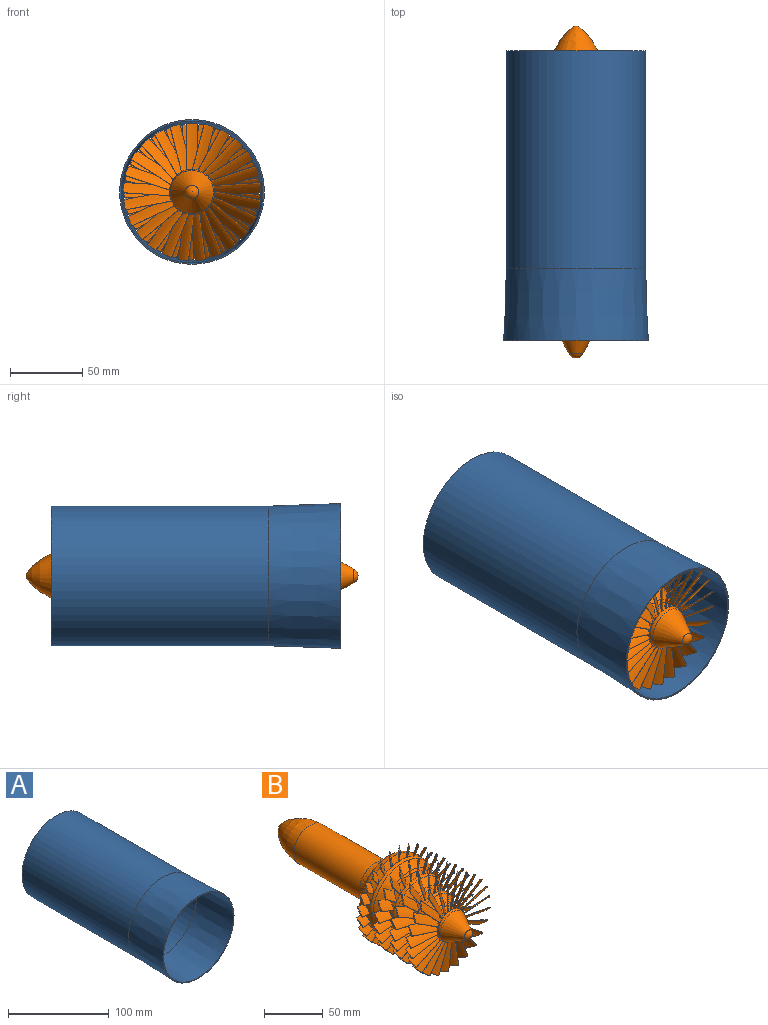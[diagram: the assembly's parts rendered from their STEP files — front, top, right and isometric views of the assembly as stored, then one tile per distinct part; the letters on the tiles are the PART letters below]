
ASSEMBLY  parts=2 mates=1
PART A: 6 faces, bbox 100x200x100 mm
  f0: cone r=50mm half-angle=2deg, axis (0,-1,0), area 15443.1mm2, adj f1,f5
  f1: plane 100x100mm, normal (0,-1,0), area 311mm2, adj f0,f2
  f2: cone r=49mm half-angle=2deg, axis (0,-1,0), area 15128.8mm2, adj f1,f3
  f3: cylinder r=47.25mm len=150mm, axis (0,-1,0), area 44535.8mm2, adj f2,f4
  f4: plane 96.51x96.51mm, normal (0,1,0), area 300mm2, adj f3,f5
  f5: cylinder r=48.25mm len=150mm, axis (0,-1,0), area 45478.3mm2, adj f0,f4
PART B: 370 faces, bbox 95.2x229.3x95.1 mm
  f0: cylinder r=22.77mm len=10.61mm, axis (0,-1,0), area 35.7mm2, adj f178,f180,f367,f369
  f1: cylinder r=22.77mm len=11.53mm, axis (0,-1,0), area 35.7mm2, adj f181,f183,f367,f369
  f2: cylinder r=22.77mm len=11.73mm, axis (0,-1,0), area 30.5mm2, adj f184,f186,f367,f368,f369
  f3: cylinder r=22.77mm len=11.19mm, axis (0,-1,0), area 35.7mm2, adj f187,f189,f367,f369
  f4: cylinder r=22.77mm len=9.95mm, axis (0,-1,0), area 35.7mm2, adj f190,f192,f367,f369
  f5: cylinder r=22.77mm len=8.53mm, axis (0,-1,0), area 35.7mm2, adj f193,f195,f367,f369
  f6: cylinder r=22.77mm len=10.27mm, axis (0,-1,0), area 35.7mm2, adj f196,f198,f367,f369
  f7: cylinder r=22.77mm len=11.37mm, axis (0,-1,0), area 35.7mm2, adj f199,f201,f367,f369
  f8: cylinder r=22.77mm len=11.75mm, axis (0,-1,0), area 35.7mm2, adj f202,f204,f367,f369
  f9: cylinder r=22.77mm len=11.39mm, axis (0,-1,0), area 35.7mm2, adj f205,f207,f367,f369
  f10: cylinder r=22.77mm len=10.32mm, axis (0,-1,0), area 35.7mm2, adj f208,f210,f367,f369
  f11: cylinder r=22.77mm len=8.6mm, axis (0,-1,0), area 35.7mm2, adj f142,f209,f367,f369
  f12: cylinder r=22.77mm len=9.9mm, axis (0,-1,0), area 35.7mm2, adj f139,f141,f367,f369
  f13: cylinder r=22.77mm len=11.16mm, axis (0,-1,0), area 35.7mm2, adj f138,f147,f367,f369
  f14: cylinder r=22.77mm len=11.72mm, axis (0,-1,0), area 30.5mm2, adj f148,f150,f367,f369
  f15: cylinder r=22.77mm len=11.55mm, axis (0,-1,0), area 35.7mm2, adj f145,f151,f367,f369
  f16: cylinder r=22.77mm len=10.65mm, axis (0,-1,0), area 35.7mm2, adj f144,f159,f367,f369
  f17: cylinder r=22.77mm len=9.08mm, axis (0,-1,0), area 35.7mm2, adj f160,f162,f367,f369
  f18: cylinder r=22.77mm len=9.48mm, axis (0,-1,0), area 35.7mm2, adj f157,f163,f367,f369
  f19: cylinder r=22.77mm len=10.91mm, axis (0,-1,0), area 35.7mm2, adj f154,f156,f367,f369
  f20: cylinder r=22.77mm len=11.65mm, axis (0,-1,0), area 35.7mm2, adj f153,f166,f367,f369
  f21: cylinder r=22.77mm len=11.66mm, axis (0,-1,0), area 35.7mm2, adj f165,f169,f367,f369
  f22: cylinder r=22.77mm len=10.94mm, axis (0,-1,0), area 35.7mm2, adj f168,f172,f367,f369
  f23: cylinder r=22.77mm len=9.53mm, axis (0,-1,0), area 35.7mm2, adj f171,f175,f367,f369
  f24: cylinder r=30.05mm len=12.66mm, axis (0,-1,0), area 48mm2, adj f328,f330,f365,f366
  f25: cylinder r=30.05mm len=13.49mm, axis (0,-1,0), area 48mm2, adj f331,f333,f365,f366
  f26: cylinder r=30.05mm len=13.47mm, axis (0,-1,0), area 48mm2, adj f334,f336,f365,f366
  f27: cylinder r=30.05mm len=12.6mm, axis (0,-1,0), area 48mm2, adj f337,f339,f365,f366
  f28: cylinder r=30.05mm len=10.95mm, axis (0,-1,0), area 48mm2, adj f340,f342,f365,f366
  f29: cylinder r=30.05mm len=10.52mm, axis (0,-1,0), area 48mm2, adj f343,f345,f365,f366
  f30: cylinder r=30.05mm len=12.33mm, axis (0,-1,0), area 48mm2, adj f346,f348,f365,f366
  f31: cylinder r=30.05mm len=13.36mm, axis (0,-1,0), area 48mm2, adj f349,f351,f365,f366
  f32: cylinder r=30.05mm len=13.55mm, axis (0,-1,0), area 48mm2, adj f352,f354,f365,f366
  f33: cylinder r=30.05mm len=12.9mm, axis (0,-1,0), area 48mm2, adj f355,f357,f365,f366
  f34: cylinder r=30.05mm len=11.43mm, axis (0,-1,0), area 48mm2, adj f358,f360,f365,f366
  f35: cylinder r=30.05mm len=9.96mm, axis (0,-1,0), area 48mm2, adj f291,f359,f365,f366
  f36: cylinder r=30.05mm len=11.94mm, axis (0,-1,0), area 48mm2, adj f288,f292,f365,f366
  f37: cylinder r=30.05mm len=13.18mm, axis (0,-1,0), area 48mm2, adj f289,f297,f365,f366
  f38: cylinder r=30.05mm len=13.59mm, axis (0,-1,0), area 48mm2, adj f298,f300,f365,f366
  f39: cylinder r=30.05mm len=13.14mm, axis (0,-1,0), area 48mm2, adj f294,f301,f365,f366
  f40: cylinder r=30.05mm len=11.87mm, axis (0,-1,0), area 48mm2, adj f295,f309,f365,f366
  f41: cylinder r=30.05mm len=9.85mm, axis (0,-1,0), area 48mm2, adj f310,f312,f365,f366
  f42: cylinder r=30.05mm len=11.51mm, axis (0,-1,0), area 48mm2, adj f306,f313,f365,f366
  f43: cylinder r=30.05mm len=12.95mm, axis (0,-1,0), area 48mm2, adj f303,f307,f365,f366
  f44: cylinder r=30.05mm len=13.56mm, axis (0,-1,0), area 48mm2, adj f304,f316,f365,f366
  f45: cylinder r=30.05mm len=13.33mm, axis (0,-1,0), area 48mm2, adj f315,f319,f365,f366
  f46: cylinder r=30.05mm len=12.26mm, axis (0,-1,0), area 48mm2, adj f318,f322,f365,f366
  f47: cylinder r=30.05mm len=10.42mm, axis (0,-1,0), area 48mm2, adj f321,f325,f365,f366
  f48: cylinder r=30.05mm len=11.04mm, axis (0,-1,0), area 48mm2, adj f324,f327,f365,f366
  f49: cylinder r=37.33mm len=74.66mm, axis (0,-1,0), area 1745mm2, adj f50,f59,f213,f214,f216,f217,f219,f220
  f50: cylinder r=37.33mm len=6.36mm, axis (0,-1,0), area 18.9mm2, adj f49,f258,f364
  f51: cylinder r=22.77mm len=9.02mm, axis (0,-1,0), area 35.7mm2, adj f174,f177,f367,f369
  f52: cylinder r=15.49mm len=30.98mm, axis (0,-1,0), area 575mm2, adj f53,f63,f64,f66,f67,f69,f70,f72
  f53: cylinder r=15.49mm len=3.79mm, axis (0,-1,0), area 6.1mm2, adj f52,f96,f100,f362
  f54: cone r=22.77mm half-angle=36.1deg, axis (0,1,0), area 1095.6mm2, adj f362,f369
  f55: cone r=15.49mm half-angle=28.8deg, axis (0,1,0), area 1297.2mm2, adj f56,f363
  f56: sphere r=5.39mm, area 94.4mm2, adj f55
  f57: revolved ~39.03x38.98mm, area 3530.5mm2, adj f58
  f58: cylinder r=19.54mm len=78.57mm, axis (0,-1,0), area 9647.2mm2, adj f57,f59
  f59: revolved ~74.66x74.66mm, area 5313.1mm2, adj f49,f58
  f60: cone r=37.33mm half-angle=36.1deg, axis (0,1,0), area 1929.3mm2, adj f364,f365
  f61: cone r=30.05mm half-angle=36.1deg, axis (0,1,0), area 1512.5mm2, adj f366,f367
  f62: cone r=49mm half-angle=2deg, axis (0,-1,0), area 4.1mm2, adj f63,f64
  f63: extruded ~33.09x14.94mm, area 321.3mm2, adj f52,f62,f64,f362
  f64: extruded ~33.12x14.9mm, area 321.3mm2, adj f52,f62,f63,f362
  f65: cone r=49mm half-angle=2deg, axis (0,-1,0), area 4.1mm2, adj f66,f67
  f66: extruded ~31.77x21.82mm, area 321.3mm2, adj f52,f65,f67,f362
  f67: extruded ~31.78x21.8mm, area 321.3mm2, adj f52,f65,f66,f362
  f68: cone r=49mm half-angle=2deg, axis (0,-1,0), area 4.1mm2, adj f69,f70
  f69: extruded ~28.45x27.33mm, area 321.3mm2, adj f52,f68,f70,f362
  f70: extruded ~28.45x27.32mm, area 321.3mm2, adj f52,f68,f69,f362
  f71: cone r=49mm half-angle=2deg, axis (0,-1,0), area 4.1mm2, adj f72,f73
  f72: extruded ~31.12x23.34mm, area 321.3mm2, adj f52,f71,f73,f362
  f73: extruded ~31.13x23.32mm, area 321.3mm2, adj f52,f71,f72,f362
  f74: cone r=49mm half-angle=2deg, axis (0,-1,0), area 4.1mm2, adj f75,f76
  f75: extruded ~32.96x16.76mm, area 321.3mm2, adj f52,f74,f76,f362
  f76: extruded ~32.98x16.73mm, area 321.3mm2, adj f52,f74,f75,f362
  f77: cone r=49mm half-angle=2deg, axis (0,-1,0), area 4.1mm2, adj f78,f79
  f78: extruded ~32.72x9.13mm, area 321.3mm2, adj f52,f77,f79,f362
  f79: extruded ~32.76x9.09mm, area 321.3mm2, adj f52,f77,f78,f362
  f80: cone r=49mm half-angle=2deg, axis (0,-1,0), area 4.1mm2, adj f81,f82
  f81: extruded ~33.1x13.05mm, area 321.3mm2, adj f52,f80,f82,f362
  f82: extruded ~33.13x13.01mm, area 321.3mm2, adj f52,f80,f81,f362
  f83: cone r=49mm half-angle=2deg, axis (0,-1,0), area 4.1mm2, adj f84,f85
  f84: extruded ~32.29x20.21mm, area 321.3mm2, adj f52,f83,f85,f362
  f85: extruded ~32.31x20.19mm, area 321.3mm2, adj f52,f83,f84,f362
  f86: cone r=49mm half-angle=2deg, axis (0,-1,0), area 4.1mm2, adj f87,f88
  f87: extruded ~29.45x26.1mm, area 321.3mm2, adj f52,f86,f88,f362
  f88: extruded ~29.46x26.09mm, area 321.3mm2, adj f52,f86,f87,f362
  f89: cone r=49mm half-angle=2deg, axis (0,-1,0), area 4.1mm2, adj f90,f91
  f90: extruded ~30.35x24.77mm, area 321.3mm2, adj f52,f89,f91,f362
  f91: extruded ~30.35x24.76mm, area 321.3mm2, adj f52,f89,f90,f362
  f92: cone r=49mm half-angle=2deg, axis (0,-1,0), area 4.1mm2, adj f93,f94
  f93: extruded ~32.69x18.52mm, area 321.3mm2, adj f52,f92,f94,f362
  f94: extruded ~32.71x18.5mm, area 321.3mm2, adj f52,f92,f93,f362
  f95: cone r=49mm half-angle=2deg, axis (0,-1,0), area 4.1mm2, adj f96,f97
  f96: extruded ~32.97x11.11mm, area 321.7mm2, adj f52,f53,f95,f97,f362
  f97: extruded ~33.01x11.07mm, area 321.3mm2, adj f52,f95,f96,f362
  f98: cone r=49mm half-angle=2deg, axis (0,-1,0), area 4.1mm2, adj f99,f100
  f99: extruded ~32.98x11.11mm, area 321.3mm2, adj f52,f98,f100,f362
  f100: extruded ~33.01x11.07mm, area 321.3mm2, adj f52,f53,f98,f99,f362
  f101: cone r=49mm half-angle=2deg, axis (0,-1,0), area 4.1mm2, adj f102,f103
  f102: extruded ~32.71x18.5mm, area 321.3mm2, adj f52,f101,f103,f362
  f103: extruded ~32.69x18.52mm, area 321.3mm2, adj f52,f101,f102,f362
  f104: cone r=49mm half-angle=2deg, axis (0,-1,0), area 4.1mm2, adj f105,f106
  f105: extruded ~30.35x24.76mm, area 321.3mm2, adj f52,f104,f106,f362
  f106: extruded ~30.35x24.77mm, area 321.3mm2, adj f52,f104,f105,f362
  f107: cone r=49mm half-angle=2deg, axis (0,-1,0), area 4.1mm2, adj f108,f109
  f108: extruded ~29.46x26.09mm, area 321.3mm2, adj f52,f107,f109,f362
  f109: extruded ~29.45x26.1mm, area 321.3mm2, adj f52,f107,f108,f362
  f110: cone r=49mm half-angle=2deg, axis (0,-1,0), area 4.1mm2, adj f111,f112
  f111: extruded ~32.31x20.19mm, area 321.3mm2, adj f52,f110,f112,f362
  f112: extruded ~32.29x20.21mm, area 321.3mm2, adj f52,f110,f111,f362
  f113: cone r=49mm half-angle=2deg, axis (0,-1,0), area 4.1mm2, adj f114,f115
  f114: extruded ~33.13x13.01mm, area 321.3mm2, adj f52,f113,f115,f362
  f115: extruded ~33.1x13.05mm, area 321.3mm2, adj f52,f113,f114,f362
  f116: cone r=49mm half-angle=2deg, axis (0,-1,0), area 4.1mm2, adj f117,f118
  f117: extruded ~32.76x9.09mm, area 321.3mm2, adj f52,f116,f118,f362
  f118: extruded ~32.72x9.13mm, area 321.3mm2, adj f52,f116,f117,f362
  f119: cone r=49mm half-angle=2deg, axis (0,-1,0), area 4.1mm2, adj f120,f121
  f120: extruded ~32.98x16.73mm, area 321.3mm2, adj f52,f119,f121,f362
  f121: extruded ~32.96x16.76mm, area 321.3mm2, adj f52,f119,f120,f362
  f122: cone r=49mm half-angle=2deg, axis (0,-1,0), area 4.1mm2, adj f123,f124
  f123: extruded ~31.13x23.32mm, area 321.3mm2, adj f52,f122,f124,f362
  f124: extruded ~31.12x23.34mm, area 321.3mm2, adj f52,f122,f123,f362
  f125: cone r=49mm half-angle=2deg, axis (0,-1,0), area 4.1mm2, adj f126,f127
  f126: extruded ~28.45x27.32mm, area 321.3mm2, adj f52,f125,f127,f362
  f127: extruded ~28.45x27.33mm, area 321.3mm2, adj f52,f125,f126,f362
  f128: cone r=49mm half-angle=2deg, axis (0,-1,0), area 4.1mm2, adj f129,f130
  f129: extruded ~31.78x21.8mm, area 321.3mm2, adj f52,f128,f130,f362
  f130: extruded ~31.77x21.82mm, area 321.3mm2, adj f52,f128,f129,f362
  f131: cone r=49mm half-angle=2deg, axis (0,-1,0), area 4.1mm2, adj f132,f133
  f132: extruded ~33.12x14.9mm, area 321.3mm2, adj f52,f131,f133,f362
  f133: extruded ~33.09x14.94mm, area 321.3mm2, adj f52,f131,f132,f362
  f134: extruded ~32.34x7.12mm, area 321.3mm2, adj f52,f135,f136,f362
  f135: extruded ~32.38x7.12mm, area 321.3mm2, adj f52,f134,f136,f362
  f136: cone r=49mm half-angle=2deg, axis (0,-1,0), area 4.1mm2, adj f134,f135
  f137: cone r=49mm half-angle=2deg, axis (0,-1,0), area 4.1mm2, adj f138,f139
  f138: extruded ~24.97x16.62mm, area 240.7mm2, adj f13,f137,f139,f367,f369
  f139: extruded ~25x16.6mm, area 240.8mm2, adj f12,f137,f138,f367,f369
  f140: cone r=49mm half-angle=2deg, axis (0,-1,0), area 4.1mm2, adj f141,f142
  f141: extruded ~23.27x20.83mm, area 240.7mm2, adj f12,f140,f142,f367,f369
  f142: extruded ~23.28x20.82mm, area 240.8mm2, adj f11,f140,f141,f367,f369
  f143: cone r=49mm half-angle=2deg, axis (0,-1,0), area 4.1mm2, adj f144,f145
  f144: extruded ~25.23x14.4mm, area 240.7mm2, adj f16,f143,f145,f367,f369
  f145: extruded ~25.27x14.37mm, area 240.8mm2, adj f15,f143,f144,f367,f369
  f146: cone r=49mm half-angle=2deg, axis (0,-1,0), area 4.1mm2, adj f147,f148
  f147: extruded ~25.15x11.34mm, area 240.8mm2, adj f13,f146,f148,f367,f369
  f148: extruded ~25.11x11.37mm, area 240.7mm2, adj f14,f146,f147,f367,f369
  f149: cone r=49mm half-angle=2deg, axis (0,-1,0), area 4.1mm2, adj f150,f151
  f150: extruded ~24.71x8.75mm, area 240.8mm2, adj f14,f149,f151,f367,f369
  f151: extruded ~24.66x8.79mm, area 240.7mm2, adj f15,f149,f150,f367,f369
  f152: cone r=49mm half-angle=2deg, axis (0,-1,0), area 4.1mm2, adj f153,f154
  f153: extruded ~25.22x12.77mm, area 240.7mm2, adj f20,f152,f154,f367,f369
  f154: extruded ~25.26x12.73mm, area 240.8mm2, adj f19,f152,f153,f367,f369
  f155: cone r=49mm half-angle=2deg, axis (0,-1,0), area 4.1mm2, adj f156,f157
  f156: extruded ~24.69x17.78mm, area 240.7mm2, adj f19,f155,f157,f367,f369
  f157: extruded ~24.72x17.77mm, area 240.8mm2, adj f18,f155,f156,f367,f369
  f158: cone r=49mm half-angle=2deg, axis (0,-1,0), area 4.1mm2, adj f159,f160
  f159: extruded ~24.24x19.09mm, area 240.8mm2, adj f16,f158,f160,f367,f369
  f160: extruded ~24.22x19.1mm, area 240.7mm2, adj f17,f158,f159,f367,f369
  f161: cone r=49mm half-angle=2deg, axis (0,-1,0), area 4.1mm2, adj f162,f163
  f162: extruded ~22.62x21.68mm, area 240.8mm2, adj f17,f161,f163,f367,f369
  f163: extruded ~22.61x21.68mm, area 240.7mm2, adj f18,f161,f162,f367,f369
  f164: cone r=49mm half-angle=2deg, axis (0,-1,0), area 4.1mm2, adj f165,f166
  f165: extruded ~24.27x7.29mm, area 240.7mm2, adj f21,f164,f166,f367,f369
  f166: extruded ~24.32x7.24mm, area 240.8mm2, adj f20,f164,f165,f367,f369
  f167: cone r=49mm half-angle=2deg, axis (0,-1,0), area 4.1mm2, adj f168,f169
  f168: extruded ~25.24x13.07mm, area 240.7mm2, adj f22,f167,f169,f367,f369
  f169: extruded ~25.28x13.04mm, area 240.8mm2, adj f21,f167,f168,f367,f369
  f170: cone r=49mm half-angle=2deg, axis (0,-1,0), area 4.1mm2, adj f171,f172
  f171: extruded ~24.62x18.03mm, area 240.7mm2, adj f23,f170,f172,f367,f369
  f172: extruded ~24.64x18.02mm, area 240.8mm2, adj f22,f170,f171,f367,f369
  f173: cone r=49mm half-angle=2deg, axis (0,-1,0), area 4.1mm2, adj f174,f175
  f174: extruded ~22.45x21.86mm, area 240.7mm2, adj f51,f173,f175,f367,f369
  f175: extruded ~22.46x21.86mm, area 240.8mm2, adj f23,f173,f174,f367,f369
  f176: cone r=49mm half-angle=2deg, axis (0,-1,0), area 4.1mm2, adj f177,f178
  f177: extruded ~24.33x18.86mm, area 240.8mm2, adj f51,f176,f178,f367,f369
  f178: extruded ~24.31x18.87mm, area 240.7mm2, adj f0,f176,f177,f367,f369
  f179: cone r=49mm half-angle=2deg, axis (0,-1,0), area 4.1mm2, adj f180,f181
  f180: extruded ~25.28x14.08mm, area 240.8mm2, adj f0,f179,f181,f367,f369
  f181: extruded ~25.24x14.11mm, area 240.7mm2, adj f1,f179,f180,f367,f369
  f182: cone r=49mm half-angle=2deg, axis (0,-1,0), area 4.1mm2, adj f183,f184
  f183: extruded ~24.63x8.42mm, area 240.8mm2, adj f1,f182,f184,f367,f369
  f184: extruded ~24.58x8.46mm, area 240.7mm2, adj f2,f182,f183,f367,f369
  f185: cone r=49mm half-angle=2deg, axis (0,-1,0), area 4.1mm2, adj f186,f187
  f186: extruded ~25.19x11.65mm, area 240.8mm2, adj f2,f185,f187,f368,f369
  f187: extruded ~25.14x11.69mm, area 240.7mm2, adj f3,f185,f186,f367,f369
  f188: cone r=49mm half-angle=2deg, axis (0,-1,0), area 4.1mm2, adj f189,f190
  f189: extruded ~24.95x16.87mm, area 240.8mm2, adj f3,f188,f190,f367,f369
  f190: extruded ~24.92x16.89mm, area 240.7mm2, adj f4,f188,f189,f367,f369
  f191: cone r=49mm half-angle=2deg, axis (0,-1,0), area 4.1mm2, adj f192,f193
  f192: extruded ~23.14x21.02mm, area 240.8mm2, adj f4,f191,f193,f367,f369
  f193: extruded ~23.13x21.02mm, area 240.7mm2, adj f5,f191,f192,f367,f369
  f194: cone r=49mm half-angle=2deg, axis (0,-1,0), area 4.1mm2, adj f195,f196
  f195: extruded ~23.85x19.88mm, area 240.8mm2, adj f5,f194,f196,f367,f369
  f196: extruded ~23.84x19.89mm, area 240.7mm2, adj f6,f194,f195,f367,f369
  f197: cone r=49mm half-angle=2deg, axis (0,-1,0), area 4.1mm2, adj f198,f199
  f198: extruded ~25.19x15.37mm, area 240.8mm2, adj f6,f197,f199,f367,f369
  f199: extruded ~25.16x15.4mm, area 240.7mm2, adj f7,f197,f198,f367,f369
  f200: cone r=49mm half-angle=2deg, axis (0,-1,0), area 4.1mm2, adj f201,f202
  f201: extruded ~24.94x9.9mm, area 240.8mm2, adj f7,f200,f202,f367,f369
  f202: extruded ~24.89x9.94mm, area 240.7mm2, adj f8,f200,f201,f367,f369
  f203: cone r=49mm half-angle=2deg, axis (0,-1,0), area 4.1mm2, adj f204,f205
  f204: extruded ~25x10.22mm, area 240.8mm2, adj f8,f203,f205,f367,f369
  f205: extruded ~24.95x10.26mm, area 240.7mm2, adj f9,f203,f204,f367,f369
  f206: cone r=49mm half-angle=2deg, axis (0,-1,0), area 4.1mm2, adj f207,f208
  f207: extruded ~25.16x15.65mm, area 240.8mm2, adj f9,f206,f208,f367,f369
  f208: extruded ~25.12x15.67mm, area 240.7mm2, adj f10,f206,f207,f367,f369
  f209: extruded ~23.72x20.1mm, area 240.7mm2, adj f11,f210,f211,f367,f369
  f210: extruded ~23.73x20.1mm, area 240.8mm2, adj f10,f209,f211,f367,f369
  f211: cone r=49mm half-angle=2deg, axis (0,-1,0), area 4.1mm2, adj f209,f210
  f212: cylinder r=47.25mm len=7.07mm, axis (0,-1,0), area 4.1mm2, adj f213,f214
  f213: extruded ~10.75x9.4mm, area 90.5mm2, adj f49,f212,f214,f364
  f214: extruded ~10.77x9.44mm, area 89.7mm2, adj f49,f212,f213,f364
  f215: cylinder r=47.25mm len=7.07mm, axis (0,-1,0), area 4.1mm2, adj f216,f217
  f216: extruded ~11.44x10.76mm, area 90.5mm2, adj f49,f215,f217,f364
  f217: extruded ~11.47x10.8mm, area 89.7mm2, adj f49,f215,f216,f364
  f218: cylinder r=47.25mm len=7.12mm, axis (0,-1,0), area 4.1mm2, adj f219,f220
  f219: extruded ~9.38x7.45mm, area 90.5mm2, adj f49,f218,f220,f364
  f220: extruded ~9.39x7.49mm, area 89.7mm2, adj f49,f218,f219,f364
  f221: cylinder r=47.25mm len=7.07mm, axis (0,-1,0), area 4.1mm2, adj f222,f223
  f222: extruded ~10.37x8.81mm, area 90.5mm2, adj f49,f221,f223,f364
  f223: extruded ~10.38x8.85mm, area 89.7mm2, adj f49,f221,f222,f364
  f224: cylinder r=47.25mm len=7.07mm, axis (0,-1,0), area 4.1mm2, adj f225,f226
  f225: extruded ~11.29x10.38mm, area 90.5mm2, adj f49,f224,f226,f364
  f226: extruded ~11.31x10.42mm, area 89.7mm2, adj f49,f224,f225,f364
  f227: cylinder r=47.25mm len=7.09mm, axis (0,-1,0), area 4.1mm2, adj f228,f229
  f228: extruded ~9.79x7.98mm, area 90.5mm2, adj f49,f227,f229,f364
  f229: extruded ~9.79x8.03mm, area 89.7mm2, adj f49,f227,f228,f364
  f230: cylinder r=47.25mm len=7.07mm, axis (0,-1,0), area 4.1mm2, adj f231,f232
  f231: extruded ~10.99x9.8mm, area 90.5mm2, adj f49,f230,f232,f364
  f232: extruded ~11.01x9.84mm, area 89.7mm2, adj f49,f230,f231,f364
  f233: cylinder r=47.25mm len=7.07mm, axis (0,-1,0), area 4.1mm2, adj f234,f235
  f234: extruded ~11.51x11.3mm, area 90.5mm2, adj f49,f233,f235,f364
  f235: extruded ~11.54x11.33mm, area 89.7mm2, adj f49,f233,f234,f364
  f236: cylinder r=47.25mm len=7.07mm, axis (0,-1,0), area 4.1mm2, adj f237,f238
  f237: extruded ~11.5x11mm, area 90.5mm2, adj f49,f236,f238,f364
  f238: extruded ~11.53x11.04mm, area 89.7mm2, adj f49,f236,f237,f364
  f239: cylinder r=47.25mm len=7.07mm, axis (0,-1,0), area 4.1mm2, adj f240,f241
  f240: extruded ~10.04x8.37mm, area 89.7mm2, adj f49,f239,f241,f364
  f241: extruded ~10.03x8.32mm, area 90.5mm2, adj f49,f239,f240,f364
  f242: cylinder r=47.25mm len=7.07mm, axis (0,-1,0), area 4.1mm2, adj f243,f244
  f243: extruded ~11.15x10.09mm, area 89.7mm2, adj f49,f242,f244,f364
  f244: extruded ~11.13x10.04mm, area 90.5mm2, adj f49,f242,f243,f364
  f245: cylinder r=47.25mm len=7.07mm, axis (0,-1,0), area 4.1mm2, adj f246,f247
  f246: extruded ~11.55x11.17mm, area 89.7mm2, adj f49,f245,f247,f364
  f247: extruded ~11.52x11.13mm, area 90.5mm2, adj f49,f245,f246,f364
  f248: cylinder r=47.25mm len=7.07mm, axis (0,-1,0), area 4.1mm2, adj f249,f250
  f249: extruded ~11.55x11.23mm, area 89.7mm2, adj f49,f248,f250,f364
  f250: extruded ~11.52x11.19mm, area 90.5mm2, adj f49,f248,f249,f364
  f251: cylinder r=47.25mm len=7.07mm, axis (0,-1,0), area 4.1mm2, adj f252,f253
  f252: extruded ~11.19x10.16mm, area 90.5mm2, adj f49,f251,f253,f364
  f253: extruded ~11.21x10.2mm, area 89.7mm2, adj f49,f251,f252,f364
  f254: cylinder r=47.25mm len=7.07mm, axis (0,-1,0), area 4.1mm2, adj f255,f256
  f255: extruded ~10.15x8.49mm, area 90.5mm2, adj f49,f254,f256,f364
  f256: extruded ~10.16x8.54mm, area 89.7mm2, adj f49,f254,f255,f364
  f257: cylinder r=47.25mm len=7.1mm, axis (0,-1,0), area 4.1mm2, adj f258,f259
  f258: extruded ~9.66x7.81mm, area 90.4mm2, adj f49,f50,f257,f259,f364
  f259: extruded ~9.66x7.85mm, area 89.7mm2, adj f49,f257,f258,f364
  f260: cylinder r=47.25mm len=7.07mm, axis (0,-1,0), area 4.1mm2, adj f261,f262
  f261: extruded ~10.92x9.67mm, area 90.5mm2, adj f49,f260,f262,f364
  f262: extruded ~10.93x9.71mm, area 89.7mm2, adj f49,f260,f261,f364
  f263: cylinder r=47.25mm len=7.07mm, axis (0,-1,0), area 4.1mm2, adj f264,f265
  f264: extruded ~11.49x10.92mm, area 90.5mm2, adj f49,f263,f265,f364
  f265: extruded ~11.52x10.96mm, area 89.7mm2, adj f49,f263,f264,f364
  f266: cylinder r=47.25mm len=7.07mm, axis (0,-1,0), area 4.1mm2, adj f267,f268
  f267: extruded ~11.49x11.34mm, area 90.5mm2, adj f49,f266,f268,f364
  f268: extruded ~11.52x11.38mm, area 89.7mm2, adj f49,f266,f267,f364
  f269: cylinder r=47.25mm len=7.07mm, axis (0,-1,0), area 4.1mm2, adj f270,f271
  f270: extruded ~11.34x10.48mm, area 90.5mm2, adj f49,f269,f271,f364
  f271: extruded ~11.36x10.52mm, area 89.7mm2, adj f49,f269,f270,f364
  f272: cylinder r=47.25mm len=7.07mm, axis (0,-1,0), area 4.1mm2, adj f273,f274
  f273: extruded ~10.47x8.96mm, area 90.5mm2, adj f49,f272,f274,f364
  f274: extruded ~10.48x9.01mm, area 89.7mm2, adj f49,f272,f273,f364
  f275: cylinder r=47.25mm len=7.13mm, axis (0,-1,0), area 4.1mm2, adj f276,f277
  f276: extruded ~9.24x7.26mm, area 90.5mm2, adj f49,f275,f277,f364
  f277: extruded ~9.25x7.31mm, area 89.7mm2, adj f49,f275,f276,f364
  f278: cylinder r=47.25mm len=7.07mm, axis (0,-1,0), area 4.1mm2, adj f279,f280
  f279: extruded ~10.66x9.26mm, area 90.5mm2, adj f49,f278,f280,f364
  f280: extruded ~10.68x9.3mm, area 89.7mm2, adj f49,f278,f279,f364
  f281: cylinder r=47.25mm len=7.07mm, axis (0,-1,0), area 4.1mm2, adj f282,f283
  f282: extruded ~11.41x10.67mm, area 90.5mm2, adj f49,f281,f283,f364
  f283: extruded ~11.44x10.71mm, area 89.7mm2, adj f49,f281,f282,f364
  f284: extruded ~11.48x11.45mm, area 89.7mm2, adj f49,f285,f286,f364
  f285: extruded ~11.45x11.42mm, area 90.5mm2, adj f49,f284,f286,f364
  f286: cylinder r=47.25mm len=7.07mm, axis (0,-1,0), area 4.1mm2, adj f284,f285
  f287: cylinder r=47.25mm len=7.07mm, axis (0,-1,0), area 4.1mm2, adj f288,f289
  f288: extruded ~17.86x12.44mm, area 162.9mm2, adj f36,f287,f289,f365,f366
  f289: extruded ~17.88x12.48mm, area 162.9mm2, adj f37,f287,f288,f365,f366
  f290: cylinder r=47.25mm len=7.07mm, axis (0,-1,0), area 4.1mm2, adj f291,f292
  f291: extruded ~17.49x15.24mm, area 162.9mm2, adj f35,f290,f292,f365,f366
  f292: extruded ~17.52x15.28mm, area 162.9mm2, adj f36,f290,f291,f365,f366
  f293: cylinder r=47.25mm len=7.07mm, axis (0,-1,0), area 4.1mm2, adj f294,f295
  f294: extruded ~17.87x12.79mm, area 162.9mm2, adj f39,f293,f295,f365,f366
  f295: extruded ~17.89x12.84mm, area 162.9mm2, adj f40,f293,f294,f365,f366
  f296: cylinder r=47.25mm len=7.09mm, axis (0,-1,0), area 4.1mm2, adj f297,f298
  f297: extruded ~17.1x8.86mm, area 162.9mm2, adj f37,f296,f298,f365,f366
  f298: extruded ~17.11x8.9mm, area 162.9mm2, adj f38,f296,f297,f365,f366
  f299: cylinder r=47.25mm len=7.07mm, axis (0,-1,0), area 4.1mm2, adj f300,f301
  f300: extruded ~17.24x9.29mm, area 162.9mm2, adj f38,f299,f301,f365,f366
  f301: extruded ~17.25x9.33mm, area 162.9mm2, adj f39,f299,f300,f365,f366
  f302: cylinder r=47.25mm len=7.07mm, axis (0,-1,0), area 4.1mm2, adj f303,f304
  f303: extruded ~17.39x9.81mm, area 162.9mm2, adj f43,f302,f304,f365,f366
  f304: extruded ~17.41x9.86mm, area 162.9mm2, adj f44,f302,f303,f365,f366
  f305: cylinder r=47.25mm len=7.07mm, axis (0,-1,0), area 4.1mm2, adj f306,f307
  f306: extruded ~17.87x13.22mm, area 162.9mm2, adj f42,f305,f307,f365,f366
  f307: extruded ~17.89x13.27mm, area 162.9mm2, adj f43,f305,f306,f365,f366
  f308: cylinder r=47.25mm len=7.07mm, axis (0,-1,0), area 4.1mm2, adj f309,f310
  f309: extruded ~17.38x15.5mm, area 162.9mm2, adj f40,f308,f310,f365,f366
  f310: extruded ~17.41x15.54mm, area 162.9mm2, adj f41,f308,f309,f365,f366
  f311: cylinder r=47.25mm len=7.07mm, axis (0,-1,0), area 4.1mm2, adj f312,f313
  f312: extruded ~17.22x15.8mm, area 162.9mm2, adj f41,f311,f313,f365,f366
  f313: extruded ~17.26x15.84mm, area 162.9mm2, adj f42,f311,f312,f365,f366
  f314: cylinder r=47.25mm len=7.11mm, axis (0,-1,0), area 4.1mm2, adj f315,f316
  f315: extruded ~16.92x8.36mm, area 162.9mm2, adj f45,f314,f316,f365,f366
  f316: extruded ~16.91x8.31mm, area 162.9mm2, adj f44,f314,f315,f365,f366
  f317: cylinder r=47.25mm len=7.07mm, axis (0,-1,0), area 4.1mm2, adj f318,f319
  f318: extruded ~17.84x12.03mm, area 162.9mm2, adj f46,f317,f319,f365,f366
  f319: extruded ~17.82x11.98mm, area 162.9mm2, adj f45,f317,f318,f365,f366
  f320: cylinder r=47.25mm len=7.07mm, axis (0,-1,0), area 4.1mm2, adj f321,f322
  f321: extruded ~17.64x14.95mm, area 162.9mm2, adj f47,f320,f322,f365,f366
  f322: extruded ~17.61x14.91mm, area 162.9mm2, adj f46,f320,f321,f365,f366
  f323: cylinder r=47.25mm len=7.07mm, axis (0,-1,0), area 4.1mm2, adj f324,f325
  f324: extruded ~16.92x16.33mm, area 162.9mm2, adj f48,f323,f325,f365,f366
  f325: extruded ~16.89x16.29mm, area 162.9mm2, adj f47,f323,f324,f365,f366
  f326: cylinder r=47.25mm len=7.07mm, axis (0,-1,0), area 4.1mm2, adj f327,f328
  f327: extruded ~17.81x13.95mm, area 162.9mm2, adj f48,f326,f328,f365,f366
  f328: extruded ~17.84x13.99mm, area 162.9mm2, adj f24,f326,f327,f365,f366
  f329: cylinder r=47.25mm len=7.07mm, axis (0,-1,0), area 4.1mm2, adj f330,f331
  f330: extruded ~17.62x10.73mm, area 162.9mm2, adj f24,f329,f331,f365,f366
  f331: extruded ~17.63x10.78mm, area 162.9mm2, adj f25,f329,f330,f365,f366
  f332: cylinder r=47.25mm len=7.13mm, axis (0,-1,0), area 4.1mm2, adj f333,f334
  f333: extruded ~16.51x7.3mm, area 162.9mm2, adj f25,f332,f334,f365,f366
  f334: extruded ~16.52x7.35mm, area 162.9mm2, adj f26,f332,f333,f365,f366
  f335: cylinder r=47.25mm len=7.07mm, axis (0,-1,0), area 4.1mm2, adj f336,f337
  f336: extruded ~17.7x11.13mm, area 162.9mm2, adj f26,f335,f337,f365,f366
  f337: extruded ~17.71x11.17mm, area 162.9mm2, adj f27,f335,f336,f365,f366
  f338: cylinder r=47.25mm len=7.07mm, axis (0,-1,0), area 4.1mm2, adj f339,f340
  f339: extruded ~17.77x14.26mm, area 162.9mm2, adj f27,f338,f340,f365,f366
  f340: extruded ~17.79x14.3mm, area 162.9mm2, adj f28,f338,f339,f365,f366
  f341: cylinder r=47.25mm len=7.07mm, axis (0,-1,0), area 4.1mm2, adj f342,f343
  f342: extruded ~16.72x16.49mm, area 162.9mm2, adj f28,f341,f343,f365,f366
  f343: extruded ~16.76x16.53mm, area 162.9mm2, adj f29,f341,f342,f365,f366
  f344: cylinder r=47.25mm len=7.07mm, axis (0,-1,0), area 4.1mm2, adj f345,f346
  f345: extruded ~17.69x14.62mm, area 162.9mm2, adj f29,f344,f346,f365,f366
  f346: extruded ~17.71x14.67mm, area 162.9mm2, adj f30,f344,f345,f365,f366
  f347: cylinder r=47.25mm len=7.07mm, axis (0,-1,0), area 4.1mm2, adj f348,f349
  f348: extruded ~17.77x11.61mm, area 162.9mm2, adj f30,f347,f349,f365,f366
  f349: extruded ~17.79x11.66mm, area 162.9mm2, adj f31,f347,f348,f365,f366
  f350: cylinder r=47.25mm len=7.12mm, axis (0,-1,0), area 4.1mm2, adj f351,f352
  f351: extruded ~16.74x7.86mm, area 162.9mm2, adj f31,f350,f352,f365,f366
  f352: extruded ~16.75x7.91mm, area 162.9mm2, adj f32,f350,f351,f365,f366
  f353: cylinder r=47.25mm len=7.07mm, axis (0,-1,0), area 4.1mm2, adj f354,f355
  f354: extruded ~17.5x10.23mm, area 162.9mm2, adj f32,f353,f355,f365,f366
  f355: extruded ~17.52x10.27mm, area 162.9mm2, adj f33,f353,f354,f365,f366
  f356: cylinder r=47.25mm len=7.07mm, axis (0,-1,0), area 4.1mm2, adj f357,f358
  f357: extruded ~17.85x13.55mm, area 162.9mm2, adj f33,f356,f358,f365,f366
  f358: extruded ~17.88x13.6mm, area 162.9mm2, adj f34,f356,f357,f365,f366
  f359: extruded ~17.12x16.06mm, area 162.9mm2, adj f35,f360,f361,f365,f366
  f360: extruded ~17.08x16.02mm, area 162.9mm2, adj f34,f359,f361,f365,f366
  f361: cylinder r=47.25mm len=7.07mm, axis (0,-1,0), area 4.1mm2, adj f359,f360
  f362: torus R=20.49mm, axis (0,-1,0), area 312.4mm2, adj f52,f53,f54,f63,f64,f66,f67,f69
  f363: torus R=10.49mm, axis (0,1,0), area 241.3mm2, adj f52,f55
  f364: torus R=32.33mm, axis (0,1,0), area 728.7mm2, adj f49,f50,f60,f213,f214,f216,f217,f219
  f365: torus R=35.05mm, axis (0,-1,0), area 600.2mm2, adj f24,f25,f26,f27,f28,f29,f30,f31
  f366: torus R=25.05mm, axis (0,1,0), area 584.8mm2, adj f24,f25,f26,f27,f28,f29,f30,f31
  f367: torus R=27.77mm, axis (0,-1,0), area 456.3mm2, adj f0,f1,f2,f3,f4,f5,f6,f7
  f368: torus R=27.77mm, axis (0,-1,0), area 0mm2, adj f2,f186,f367
  f369: torus R=17.77mm, axis (0,1,0), area 440.9mm2, adj f0,f1,f2,f3,f4,f5,f6,f7
PLACE A t=(0,-9.73,0)mm
PLACE B t=(0,-11.37,0)mm
MATE revolute B.f0 <-> A.f0  axis (0,1,0) through (0,-29.73,0)mm
